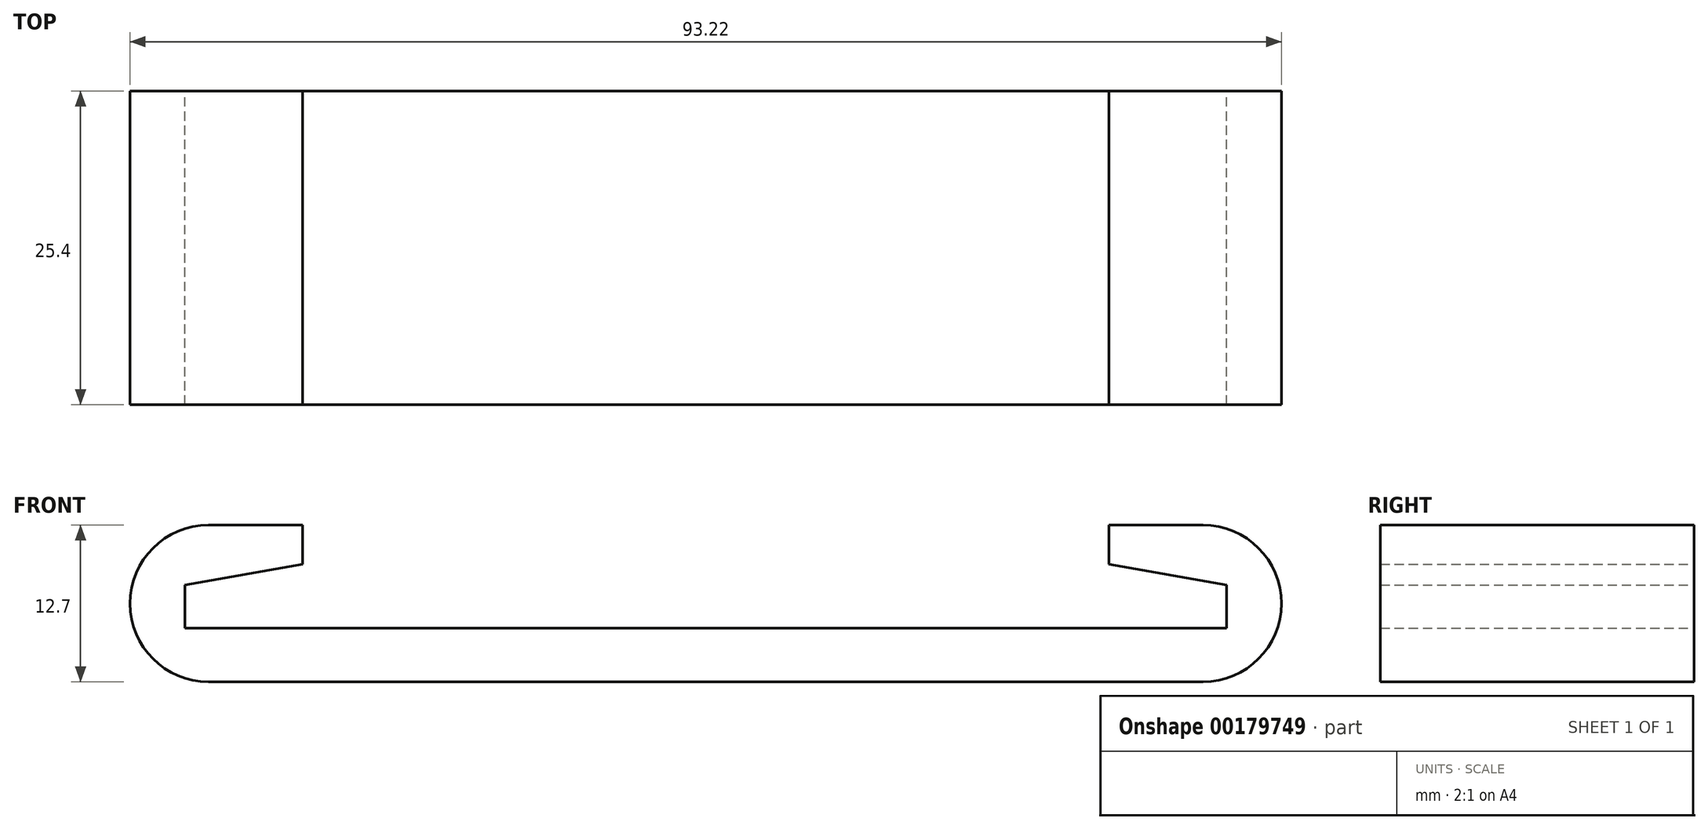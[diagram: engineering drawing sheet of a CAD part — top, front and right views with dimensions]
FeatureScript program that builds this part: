
annotation { "Feature Type Name" : "Feature", "Feature Type Description" : "" }
export const myFeature = defineFeature(function(context is Context, id is Id, definition is map)
    precondition{}
    {
        {
            var Q0;
            Q0=qCreatedBy(makeId("Front.planeOp"),FACE);
            var sketch = newSketch(context, id + "F0", { "sketchPlane" : qUnion([Q0])});
            skLineSegment(sketch, "E0", {"start": v(0, 0) * mm, "end": v(-46.6, 0) * mm});
            skLineSegment(sketch, "E1", {"start": v(-46.6, 0) * mm, "end": v(-46.6, 12.7) * mm});
            skLineSegment(sketch, "E2", {"start": v(-46.6, 12.7) * mm, "end": v(-32.64, 12.7) * mm});
            skLineSegment(sketch, "E3", {"start": v(-32.64, 12.7) * mm, "end": v(-32.64, 9.53) * mm});
            skLineSegment(sketch, "E4", {"start": v(-32.64, 9.53) * mm, "end": v(-42.16, 7.85) * mm});
            skLineSegment(sketch, "E5", {"start": v(-42.16, 7.85) * mm, "end": v(-42.16, 4.34) * mm});
            skLineSegment(sketch, "E6", {"start": v(-42.16, 4.34) * mm, "end": v(0, 4.34) * mm});
            skLineSegment(sketch, "E7", {"start": v(0, 4.34) * mm, "end": v(0, 0) * mm});
            skSolve(sketch);
        }
        {
            var Q0;
            Q0=makeQuery(id+"F0.imprint","IMPRINT",FACE,{"disambiguationData":[TD([[makeQuery(id+"F0.imprint","IMPRINT",EDGE,{"derivedFrom":sQuery(id+"F0.wireOp",EDGE,"E0")}),-1.0]])]});
            extrude(context, id + "F1", {"entities" : qUnion([Q0]), "depth" : 25.4 * mm});
        }
        {
            var Q0;
            Q0=makeQuery(id+"F1.opExtrude","SWEPT_EDGE",EDGE,{"disambiguationData":[OSD([sQuery(id+"F0.wireOp",EDGE,"E1"),sQuery(id+"F0.wireOp",EDGE,"E2")])]});
            var Q1;
            Q1=makeQuery(id+"F1.opExtrude","SWEPT_EDGE",EDGE,{"disambiguationData":[OSD([sQuery(id+"F0.wireOp",EDGE,"E0"),sQuery(id+"F0.wireOp",EDGE,"E1")])]});
            fillet(context, id + "F2", {"entities" : qUnion([Q0, Q1]), "radius" : 6.35 * mm, "tangentPropagation" : true, "allowEdgeOverflow" : false});
        }
        {
            var Q0;
            Q0=makeQuery(id+"F1.opExtrude","SWEPT_BODY",BODY,{"disambiguationData":[OSD([sQuery(id+"F0.wireOp",EDGE,"E0"),sQuery(id+"F0.wireOp",EDGE,"E1"),sQuery(id+"F0.wireOp",EDGE,"E2"),sQuery(id+"F0.wireOp",EDGE,"E3"),sQuery(id+"F0.wireOp",EDGE,"E4"),sQuery(id+"F0.wireOp",EDGE,"E5"),sQuery(id+"F0.wireOp",EDGE,"E6"),sQuery(id+"F0.wireOp",EDGE,"E7")])]});
            var Q1;
            Q1=makeQuery(id+"F1.opExtrude","SWEPT_FACE",FACE,{"disambiguationData":[OSD([sQuery(id+"F0.wireOp",EDGE,"E7")])]});
            mirror(context, id + "F3", {"operationType" : NewBodyOperationType.ADD, "entities" : qUnion([Q0]), "mirrorPlane" : qUnion([Q1])});
        }
    });
